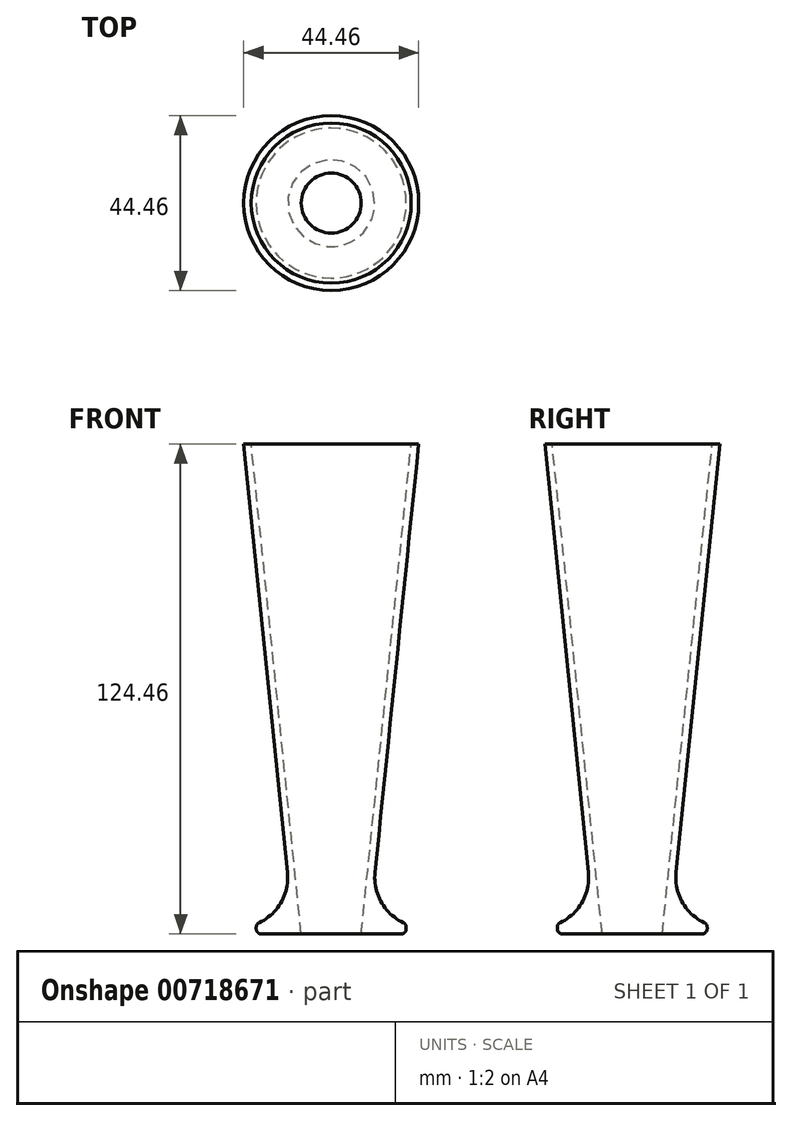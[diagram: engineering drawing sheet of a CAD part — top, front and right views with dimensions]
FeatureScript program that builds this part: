
annotation { "Feature Type Name" : "Feature", "Feature Type Description" : "" }
export const myFeature = defineFeature(function(context is Context, id is Id, definition is map)
    precondition{}
    {
        {
            var Q0;
            Q0=qCreatedBy(makeId("Top.planeOp"),FACE);
            var sketch = newSketch(context, id + "F0", { "sketchPlane" : qUnion([Q0])});
            skCircle(sketch, "E0", {"center": v(0, 0) * mm, "radius": 9.53 * mm});
            skSolve(sketch);
        }
        {
            var Q0;
            Q0=qCreatedBy(makeId("Top.planeOp"),FACE);
            cPlane(context, id + "F1", {"entities" : qUnion([Q0]), "cplaneType" : CPlaneType.OFFSET, "offset" : 124.46 * mm, "width" : 152.4 * mm, "height" : 152.4 * mm});
        }
        {
            var Q0;
            Q0=qCreatedBy(id+"F1.planeOp",FACE);
            var sketch = newSketch(context, id + "F2", { "sketchPlane" : qUnion([Q0])});
            skCircle(sketch, "E1", {"center": v(0, 0) * mm, "radius": 22.23 * mm});
            skSolve(sketch);
        }
        {
            var Q0;
            Q0=makeQuery(id+"F0.imprint","IMPRINT",FACE,{"disambiguationData":[TD([[makeQuery(id+"F0.imprint","IMPRINT",EDGE,{"derivedFrom":sQuery(id+"F0.wireOp",EDGE,"E0")}),1.0]])]});
            var Q1;
            Q1=makeQuery(id+"F2.imprint","IMPRINT",FACE,{"disambiguationData":[TD([[makeQuery(id+"F2.imprint","IMPRINT",EDGE,{"derivedFrom":sQuery(id+"F2.wireOp",EDGE,"E1")}),1.0]])]});
            loft(context, id + "F3", {"sheetProfilesArray" : [{ "sheetProfileEntities" : qUnion([Q0]) }, { "sheetProfileEntities" : qUnion([Q1]) }]});
        }
        {
            var Q0;
            Q0=makeQuery(id+"F3.opLoft","CAP_FACE",FACE,{"disambiguationData":[OSD([makeQuery(id+"F2.imprint","IMPRINT",FACE,{"disambiguationData":[TD([[makeQuery(id+"F2.imprint","IMPRINT",EDGE,{"derivedFrom":sQuery(id+"F2.wireOp",EDGE,"E1")}),1.0]])]})])],"isStart":true});
            var sketch = newSketch(context, id + "F4", { "sketchPlane" : qUnion([Q0])});
            skCircle(sketch, "E2", {"center": v(0, 0) * mm, "radius": 20.32 * mm});
            skSolve(sketch);
        }
        {
            var Q0;
            Q0=makeQuery(id+"F3.opLoft","CAP_FACE",FACE,{"disambiguationData":[OSD([makeQuery(id+"F0.imprint","IMPRINT",FACE,{"disambiguationData":[TD([[makeQuery(id+"F0.imprint","IMPRINT",EDGE,{"derivedFrom":sQuery(id+"F0.wireOp",EDGE,"E0")}),1.0]])]})])],"isStart":true});
            var sketch = newSketch(context, id + "F5", { "sketchPlane" : qUnion([Q0])});
            skCircle(sketch, "E3", {"center": v(0, 0) * mm, "radius": 7.62 * mm});
            skSolve(sketch);
        }
        {
            var Q0;
            Q0=qCreatedBy(makeId("Top.planeOp"),FACE);
            var sketch = newSketch(context, id + "F6", { "sketchPlane" : qUnion([Q0])});
            skCircle(sketch, "E4", {"center": v(0, 0) * mm, "radius": 19.05 * mm});
            skSolve(sketch);
        }
        {
            var Q0;
            Q0=makeQuery(id+"F6.imprint","IMPRINT",FACE,{"disambiguationData":[TD([[makeQuery(id+"F6.imprint","IMPRINT",EDGE,{"derivedFrom":sQuery(id+"F6.wireOp",EDGE,"E4")}),1.0]])]});
            extrude(context, id + "F7", {"entities" : qUnion([Q0]), "operationType" : NewBodyOperationType.ADD, "depth" : 2.54 * mm, "offsetDistance" : 25.4 * mm});
        }
        {
            var Q1;
            Q1=makeQuery(id+"F5.imprint","IMPRINT",FACE,{"disambiguationData":[TD([[makeQuery(id+"F5.imprint","IMPRINT",EDGE,{"derivedFrom":sQuery(id+"F5.wireOp",EDGE,"E3")}),1.0]])]});
            var Q2;
            Q2=makeQuery(id+"F4.imprint","IMPRINT",FACE,{"disambiguationData":[TD([[makeQuery(id+"F4.imprint","IMPRINT",EDGE,{"derivedFrom":sQuery(id+"F4.wireOp",EDGE,"E2")}),1.0]])]});
            loft(context, id + "F8", {"operationType" : NewBodyOperationType.REMOVE, "sheetProfilesArray" : [{ "sheetProfileEntities" : qUnion([Q1]) }, { "sheetProfileEntities" : qUnion([Q2]) }]});
        }
        {
            var Q0;
            Q0=makeQuery(id+"F7.boolean.opBoolean","INTERSECT",EDGE,{"derivedFrom":[makeQuery(id+"F3.opLoft","SWEPT_FACE",FACE,{"disambiguationData":[OSD([sQuery(id+"F0.wireOp",EDGE,"E0"),sQuery(id+"F2.wireOp",EDGE,"E1")])]}),makeQuery(id+"F7.opExtrude","CAP_FACE",FACE,{"disambiguationData":[OSD([sQuery(id+"F6.wireOp",EDGE,"E4")])],"isStart":false})]});
            fillet(context, id + "F9", {"entities" : qUnion([Q0]), "radius" : 12.7 * mm, "tangentPropagation" : true, "allowEdgeOverflow" : false});
        }
        {
            var Q0;
            {var subQ0=sQuery(id+"F6.wireOp",EDGE,"E4");Q0=makeQuery(id+"F9.opFillet","BLEND_EDGE",EDGE,{"blendedFrom":[makeQuery(id+"F7.boolean.opBoolean","INTERSECT",EDGE,{"derivedFrom":[makeQuery(id+"F3.opLoft","SWEPT_FACE",FACE,{"disambiguationData":[OSD([sQuery(id+"F0.wireOp",EDGE,"E0"),sQuery(id+"F2.wireOp",EDGE,"E1")])]}),makeQuery(id+"F7.opExtrude","CAP_FACE",FACE,{"disambiguationData":[OSD([subQ0])],"isStart":false})]}),makeQuery(id+"F7.opExtrude","SWEPT_FACE",FACE,{"disambiguationData":[OSD([subQ0])]})],"blendedInto":[makeQuery(id+"F7.opExtrude","SWEPT_FACE",FACE,{"disambiguationData":[OSD([subQ0])]})]});}
            var Q1;
            Q1=makeQuery(id+"F7.opExtrude","CAP_EDGE",EDGE,{"disambiguationData":[OSD([sQuery(id+"F6.wireOp",EDGE,"E4")])],"isStart":true});
            fillet(context, id + "F10", {"entities" : qUnion([Q0, Q1]), "radius" : 1.27 * mm, "tangentPropagation" : true, "allowEdgeOverflow" : false});
        }
    });
